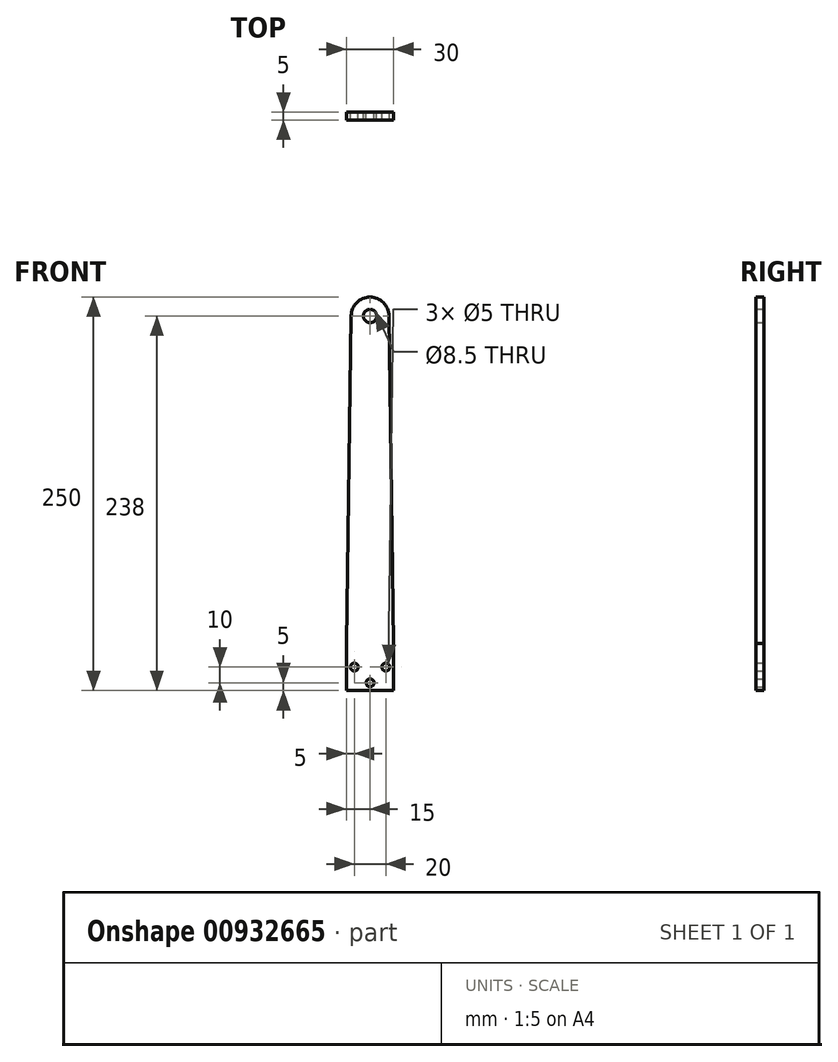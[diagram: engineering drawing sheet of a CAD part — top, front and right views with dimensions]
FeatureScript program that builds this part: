
annotation { "Feature Type Name" : "Feature", "Feature Type Description" : "" }
export const myFeature = defineFeature(function(context is Context, id is Id, definition is map)
    precondition{}
    {
        {
            var Q0;
            Q0=qCreatedBy(makeId("Front.planeOp"),FACE);
            var sketch = newSketch(context, id + "F0", { "sketchPlane" : qUnion([Q0])});
            skLineSegment(sketch, "E0.top", {"start": v(-15, -125) * mm, "end": v(15, -125) * mm});
            skLineSegment(sketch, "E0.left", {"start": v(-15, -95) * mm, "end": v(-15, -125) * mm});
            skLineSegment(sketch, "E0.right", {"start": v(15, -95) * mm, "end": v(15, -125) * mm});
            skPoint(sketch, "E0.middle", {"position": v(0, 0) * mm});
            skCircle(sketch, "E1", {"center": v(0, 113) * mm, "radius": 4.25 * mm});
            skPoint(sketch, "E1.centerSnap0", {"position": v(0, 125) * mm});
            skArc(sketch, "E2", {"start": v(12, 113.17) * mm, "mid": v(8.42, 121.55) * mm, "end": v(0, 125) * mm});
            skPoint(sketch, "E3", {"position": v(-15, -95) * mm});
            skPoint(sketch, "E4", {"position": v(15, -95) * mm});
            skLineSegment(sketch, "E5", {"start": v(-15, -95) * mm, "end": v(-12, 113.17) * mm});
            skLineSegment(sketch, "E6", {"start": v(15, -95) * mm, "end": v(12, 113.17) * mm});
            skArc(sketch, "E7", {"start": v(12, 113.17) * mm, "mid": v(0, 125) * mm, "end": v(-12, 113.17) * mm});
            skPoint(sketch, "E8.center.orphan", {"position": v(-10, -110) * mm});
            skCircle(sketch, "E9", {"center": v(-10, -110) * mm, "radius": 2.5 * mm});
            skPoint(sketch, "E10.center.orphan", {"position": v(10, -110) * mm});
            skCircle(sketch, "E11", {"center": v(10, -110) * mm, "radius": 2.5 * mm});
            skCircle(sketch, "E12", {"center": v(0, -120) * mm, "radius": 2.5 * mm});
            skSolve(sketch);
        }
        {
            var Q0;
            Q0=makeQuery(id+"F0.imprint","IMPRINT",FACE,{"disambiguationData":[TD([[makeQuery(id+"F0.imprint","IMPRINT",EDGE,{"derivedFrom":sQuery(id+"F0.wireOp",EDGE,"E0.top")}),1.0]])]});
            extrude(context, id + "F1", {"entities" : qUnion([Q0]), "depth" : 5 * mm, "offsetDistance" : 25 * mm});
        }
    });
